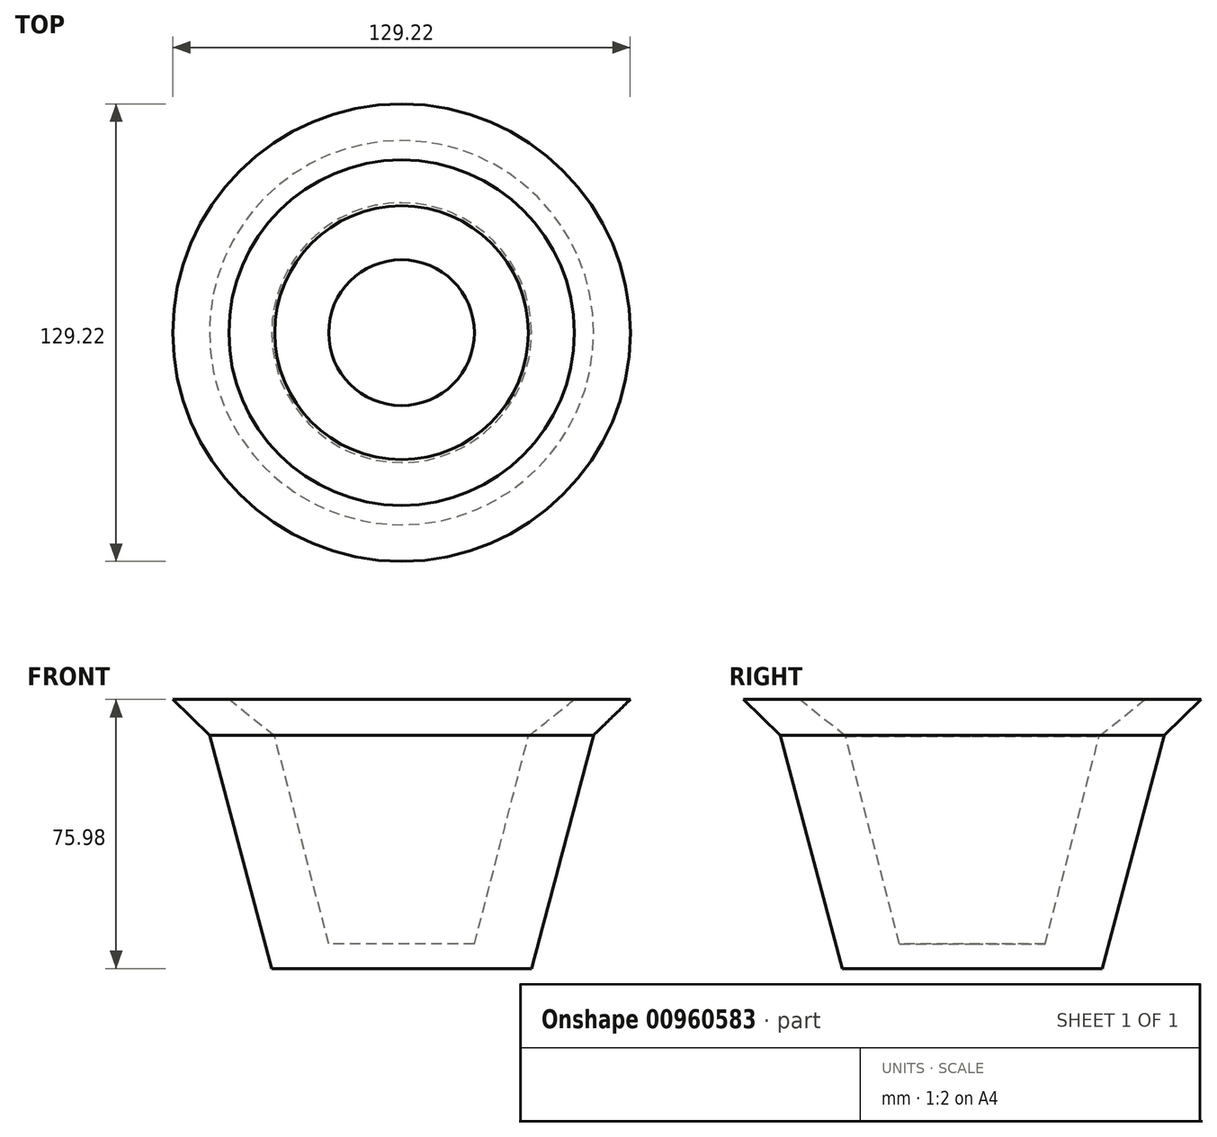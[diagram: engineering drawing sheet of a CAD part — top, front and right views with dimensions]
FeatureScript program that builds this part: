
annotation { "Feature Type Name" : "Feature", "Feature Type Description" : "" }
export const myFeature = defineFeature(function(context is Context, id is Id, definition is map)
    precondition{}
    {
        {
            var Q0;
            Q0=qCreatedBy(makeId("Front.planeOp"),FACE);
            var sketch = newSketch(context, id + "F0", { "sketchPlane" : qUnion([Q0])});
            skLineSegment(sketch, "E0", {"start": v(0, 67.78) * mm, "end": v(0, -68.35) * mm});
            skLineSegment(sketch, "E1", {"start": v(0, -55.4) * mm, "end": v(-36.7, -55.4) * mm});
            skLineSegment(sketch, "E2", {"start": v(-36.7, -55.4) * mm, "end": v(-54.25, 10.5) * mm});
            skLineSegment(sketch, "E3", {"start": v(-54.25, 10.5) * mm, "end": v(-64.61, 20.58) * mm});
            skLineSegment(sketch, "E4", {"start": v(-64.61, 20.58) * mm, "end": v(-48.78, 20.58) * mm});
            skLineSegment(sketch, "E5", {"start": v(-48.78, 20.58) * mm, "end": v(-35.83, 10.22) * mm});
            skLineSegment(sketch, "E6", {"start": v(-35.83, 10.22) * mm, "end": v(-20.58, -48.5) * mm});
            skLineSegment(sketch, "E7", {"start": v(-20.58, -48.5) * mm, "end": v(0, -48.5) * mm});
            skLineSegment(sketch, "E8", {"start": v(0, -48.5) * mm, "end": v(0, -55.4) * mm});
            skSolve(sketch);
        }
        {
            var Q0;
            Q0=makeQuery(id+"F0.imprint","IMPRINT",FACE,{"disambiguationData":[TD([[makeQuery(id+"F0.imprint","IMPRINT",EDGE,{"derivedFrom":sQuery(id+"F0.wireOp",EDGE,"E1")}),-1.0]])]});
            var Q1;
            Q1=sQuery(id+"F0.wireOp",EDGE,"E0");
            revolve(context, id + "F1", {"surfaceOperationType" : NewSurfaceOperationType.NEW, "entities" : qUnion([Q0]), "axis" : qUnion([Q1]), "revolveType" : RevolveType.FULL});
        }
    });
